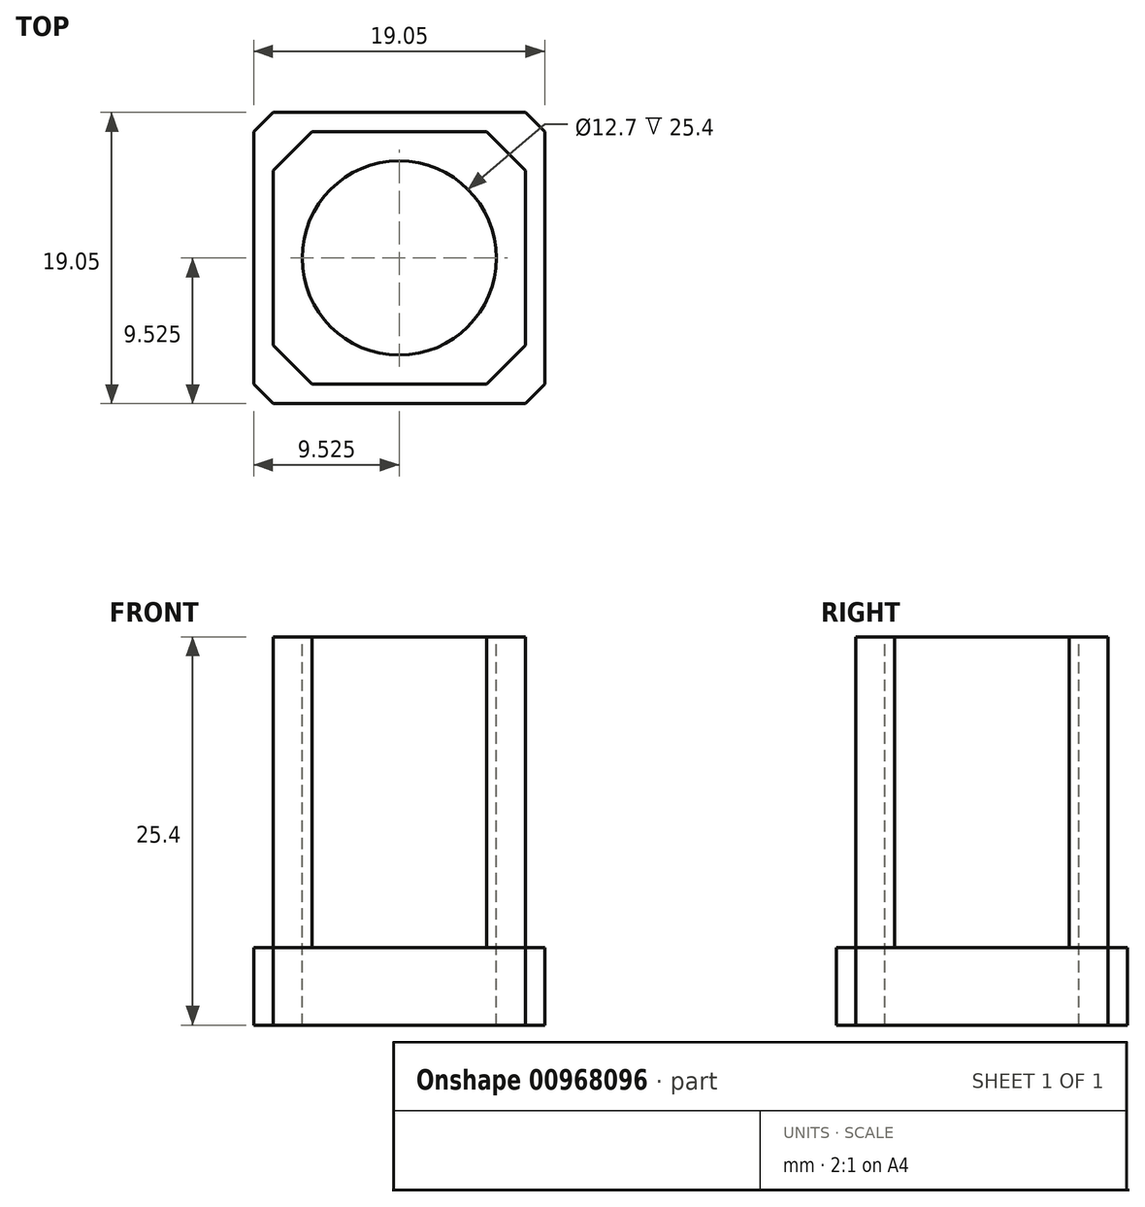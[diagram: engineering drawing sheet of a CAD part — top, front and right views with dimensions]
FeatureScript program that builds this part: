
annotation { "Feature Type Name" : "Feature", "Feature Type Description" : "" }
export const myFeature = defineFeature(function(context is Context, id is Id, definition is map)
    precondition{}
    {
        {
            var Q0;
            Q0=qCreatedBy(makeId("Top.planeOp"),FACE);
            var sketch = newSketch(context, id + "F0", { "sketchPlane" : qUnion([Q0])});
            skLineSegment(sketch, "E0.bottom", {"start": v(0, 0) * mm, "end": v(19.05, 0) * mm});
            skLineSegment(sketch, "E0.top", {"start": v(0, 19.05) * mm, "end": v(19.05, 19.05) * mm});
            skLineSegment(sketch, "E0.left", {"start": v(0, 0) * mm, "end": v(0, 19.05) * mm});
            skLineSegment(sketch, "E0.right", {"start": v(19.05, 0) * mm, "end": v(19.05, 19.05) * mm});
            skSolve(sketch);
        }
        {
            var Q0;
            Q0 = qSketchRegion(id + "F0", true);
            extrude(context, id + "F1", {"entities" : qUnion([Q0]), "depth" : 5.08 * mm, "offsetDistance" : 25.4 * mm});
        }
        {
            var Q0;
            Q0=makeQuery(id+"F1.opExtrude","CAP_FACE",FACE,{"disambiguationData":[OSD([sQuery(id+"F0.wireOp",EDGE,"E0.bottom"),sQuery(id+"F0.wireOp",EDGE,"E0.top"),sQuery(id+"F0.wireOp",EDGE,"E0.left"),sQuery(id+"F0.wireOp",EDGE,"E0.right")])],"isStart":false});
            var sketch = newSketch(context, id + "F2", { "sketchPlane" : qUnion([Q0])});
            skCircle(sketch, "E1.cCircle", {"center": v(9.53, 9.53) * mm, "radius": 8.25 * mm, "construction": true});
            skLineSegment(sketch, "E1.0", {"start": v(17.78, 17.78) * mm, "end": v(17.78, 1.27) * mm});
            skLineSegment(sketch, "E1.1", {"start": v(17.78, 1.27) * mm, "end": v(1.27, 1.27) * mm});
            skLineSegment(sketch, "E1.2", {"start": v(1.27, 1.27) * mm, "end": v(1.27, 17.78) * mm});
            skLineSegment(sketch, "E1.3", {"start": v(1.27, 17.78) * mm, "end": v(17.78, 17.78) * mm});
            skPoint(sketch, "E1.0.midPoint", {"position": v(17.78, 9.53) * mm});
            skSolve(sketch);
        }
        {
            var Q0;
            Q0 = qSketchRegion(id + "F2", true);
            extrude(context, id + "F3", {"entities" : qUnion([Q0]), "operationType" : NewBodyOperationType.ADD, "depth" : 20.32 * mm, "offsetDistance" : 25.4 * mm});
        }
        {
            var Q0;
            Q0=makeQuery(id+"F3.opExtrude","CAP_FACE",FACE,{"disambiguationData":[OSD([sQuery(id+"F2.wireOp",EDGE,"E1.0"),sQuery(id+"F2.wireOp",EDGE,"E1.1"),sQuery(id+"F2.wireOp",EDGE,"E1.2"),sQuery(id+"F2.wireOp",EDGE,"E1.3")])],"isStart":false});
            var sketch = newSketch(context, id + "F4", { "sketchPlane" : qUnion([Q0])});
            skLineSegment(sketch, "E2", {"start": v(17.78, 1.27) * mm, "end": v(1.27, 17.78) * mm});
            skLineSegment(sketch, "E3", {"start": v(1.27, 17.78) * mm, "end": v(1.27, 1.27) * mm});
            skLineSegment(sketch, "E4", {"start": v(1.27, 1.27) * mm, "end": v(17.78, 17.78) * mm});
            skLineSegment(sketch, "E5", {"start": v(17.78, 17.78) * mm, "end": v(17.78, 1.27) * mm});
            skCircle(sketch, "E6", {"center": v(9.53, 9.53) * mm, "radius": 6.35 * mm});
            skSolve(sketch);
        }
        {
            var Q0;
            {var subQ0=sQuery(id+"F4.wireOp",EDGE,"E4");var subQ1=sQuery(id+"F4.wireOp",EDGE,"E2");var subQ2=makeQuery(id+"F4.imprint","INTERSECT",VERTEX,{"derivedFrom":[subQ1,subQ0]});Q0=makeQuery(id+"F4.imprint","IMPRINT",FACE,{"disambiguationData":[TD([[makeQuery(id+"F4.imprint","IMPRINT",EDGE,{"disambiguationData":[TD([[subQ2,-1.0]])],"derivedFrom":subQ1}),1.0]])]});}
            var Q1;
            {var subQ0=sQuery(id+"F4.wireOp",EDGE,"E4");var subQ1=sQuery(id+"F4.wireOp",EDGE,"E2");var subQ2=makeQuery(id+"F4.imprint","INTERSECT",VERTEX,{"derivedFrom":[subQ1,subQ0]});Q1=makeQuery(id+"F4.imprint","IMPRINT",FACE,{"disambiguationData":[TD([[makeQuery(id+"F4.imprint","IMPRINT",EDGE,{"disambiguationData":[TD([[subQ2,-1.0]])],"derivedFrom":subQ1}),-1.0]])]});}
            var Q2;
            {var subQ0=sQuery(id+"F4.wireOp",EDGE,"E6");var subQ1=sQuery(id+"F4.wireOp",EDGE,"E2");var subQ2=makeQuery(id+"F4.imprint","INTERSECT",VERTEX,{"disambiguationData":[OD(0.0)],"derivedFrom":[subQ1,subQ0]});Q2=makeQuery(id+"F4.imprint","IMPRINT",FACE,{"disambiguationData":[TD([[makeQuery(id+"F4.imprint","IMPRINT",EDGE,{"disambiguationData":[TD([[subQ2,-1.0]])],"derivedFrom":subQ1}),-1.0]])]});}
            var Q3;
            {var subQ0=sQuery(id+"F4.wireOp",EDGE,"E6");var subQ1=sQuery(id+"F4.wireOp",EDGE,"E2");var subQ2=makeQuery(id+"F4.imprint","INTERSECT",VERTEX,{"disambiguationData":[OD(0.0)],"derivedFrom":[subQ1,subQ0]});Q3=makeQuery(id+"F4.imprint","IMPRINT",FACE,{"disambiguationData":[TD([[makeQuery(id+"F4.imprint","IMPRINT",EDGE,{"disambiguationData":[TD([[subQ2,-1.0]])],"derivedFrom":subQ1}),1.0]])]});}
            extrude(context, id + "F5", {"entities" : qUnion([Q0, Q1, Q2, Q3]), "operationType" : NewBodyOperationType.REMOVE, "oppositeDirection" : true, "depth" : 25.4 * mm, "offsetDistance" : 25.4 * mm});
        }
        {
            var Q0;
            Q0=makeQuery(id+"F3.opExtrude","SWEPT_EDGE",EDGE,{"disambiguationData":[OSD([sQuery(id+"F2.wireOp",EDGE,"E1.0"),sQuery(id+"F2.wireOp",EDGE,"E1.3")])]});
            var Q1;
            Q1=makeQuery(id+"F3.opExtrude","SWEPT_EDGE",EDGE,{"disambiguationData":[OSD([sQuery(id+"F2.wireOp",EDGE,"E1.2"),sQuery(id+"F2.wireOp",EDGE,"E1.3")])]});
            var Q2;
            Q2=makeQuery(id+"F3.opExtrude","SWEPT_EDGE",EDGE,{"disambiguationData":[OSD([sQuery(id+"F2.wireOp",EDGE,"E1.1"),sQuery(id+"F2.wireOp",EDGE,"E1.2")])]});
            var Q3;
            Q3=makeQuery(id+"F3.opExtrude","SWEPT_EDGE",EDGE,{"disambiguationData":[OSD([sQuery(id+"F2.wireOp",EDGE,"E1.0"),sQuery(id+"F2.wireOp",EDGE,"E1.1")])]});
            chamfer(context, id + "F6", {"entities" : qUnion([Q0, Q1, Q2, Q3]), "width" : 2.54 * mm, "tangentPropagation" : true});
        }
        {
            var Q0;
            Q0=makeQuery(id+"F1.opExtrude","SWEPT_EDGE",EDGE,{"disambiguationData":[OSD([sQuery(id+"F0.wireOp",EDGE,"E0.bottom"),sQuery(id+"F0.wireOp",EDGE,"E0.left")])]});
            var Q1;
            Q1=makeQuery(id+"F1.opExtrude","SWEPT_EDGE",EDGE,{"disambiguationData":[OSD([sQuery(id+"F0.wireOp",EDGE,"E0.top"),sQuery(id+"F0.wireOp",EDGE,"E0.left")])]});
            var Q2;
            Q2=makeQuery(id+"F1.opExtrude","SWEPT_EDGE",EDGE,{"disambiguationData":[OSD([sQuery(id+"F0.wireOp",EDGE,"E0.top"),sQuery(id+"F0.wireOp",EDGE,"E0.right")])]});
            var Q3;
            Q3=makeQuery(id+"F1.opExtrude","SWEPT_EDGE",EDGE,{"disambiguationData":[OSD([sQuery(id+"F0.wireOp",EDGE,"E0.bottom"),sQuery(id+"F0.wireOp",EDGE,"E0.right")])]});
            chamfer(context, id + "F7", {"entities" : qUnion([Q0, Q1, Q2, Q3]), "width" : 1.27 * mm, "tangentPropagation" : true});
        }
    });
